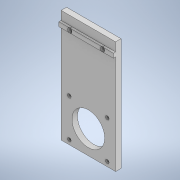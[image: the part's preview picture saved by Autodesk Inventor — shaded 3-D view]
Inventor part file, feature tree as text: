
AUTODESK INVENTOR PART (.ipt)
format: ipt  version: 2021 (Build 250183000, 183)  size: 166,400 bytes
history: native  units: mm
features: extrude x3, sketch x3, projected_geometry x2
ambient origin geometry x8: Origin, YZ Plane, XZ Plane, XY Plane, X Axis, Y Axis, Z Axis, Center Point
bodies: Solid1 (feature_tree)
feature tree (8):
  extrude  "Extrusion1"  Depth=206.0mm
  extrude  "Extrusion2"  Depth=60.0mm
  extrude  "Extrusion3"  Depth=8.0mm
  sketch  "Sketch1"  dims[d0=100.0mm d1=206.0mm]
  sketch  "Sketch2"  dims[d2=60.0mm d3=43.0mm]
  projected_geometry  "Projected Loop1"
  sketch  "Sketch3"  dims[d4=8.0mm d5=8.0mm d6=20.0mm d7=20.0mm d8=20.0mm d9=20.0mm d10=6.5mm d11=6.5mm d12=6.5mm d13=6.5mm d14=69.6mm d15=69.6mm d16=69.6mm d17=69.6mm d18=0.0mm d19=0.0mm d20=34.8mm d21=34.8mm d22=109.0mm d23=20.0mm d24=0.0mm d25=4.0mm d26=4.0mm d27=4.0mm d28=0.0mm d29=6.0mm d30=0.0mm]
  projected_geometry  "Projected Loop2"
